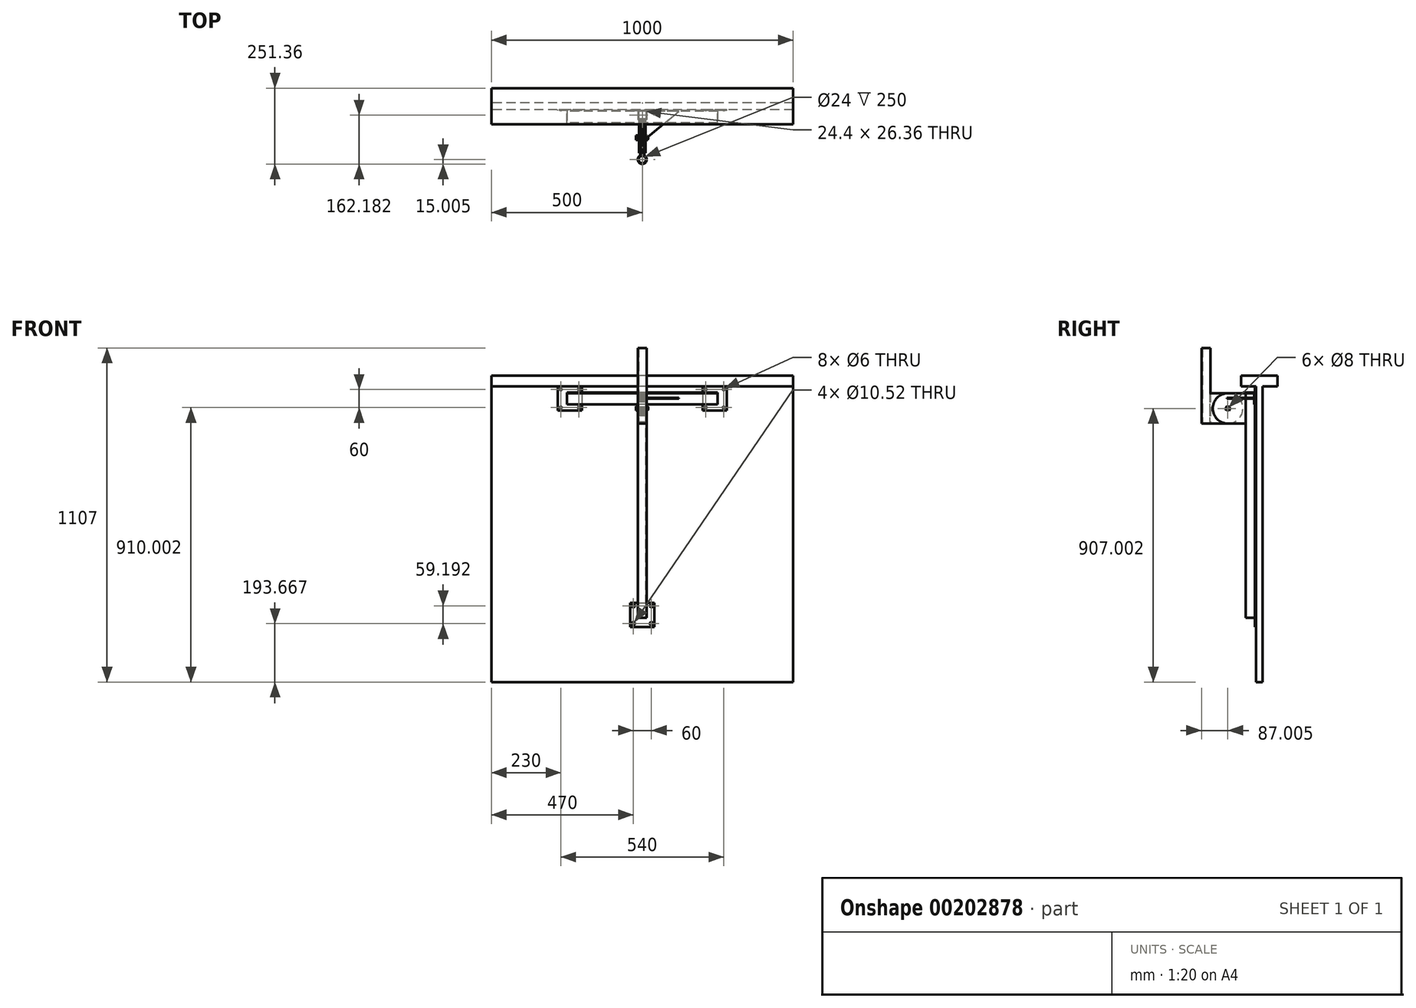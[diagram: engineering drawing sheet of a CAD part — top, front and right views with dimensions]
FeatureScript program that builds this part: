
annotation { "Feature Type Name" : "Feature", "Feature Type Description" : "" }
export const myFeature = defineFeature(function(context is Context, id is Id, definition is map)
    precondition{}
    {
        {
            assignVariable(context, id + "F0", {"name" : "PlateWidth", "anyValue" : 100});
        }
        {
            var Q0;
            Q0=qCreatedBy(makeId("Right.planeOp"),FACE);
            var sketch = newSketch(context, id + "F1", { "sketchPlane" : qUnion([Q0])});
            skLineSegment(sketch, "E0", {"start": v(0, 214.68) * mm, "end": v(0, -692.13) * mm, "construction": true});
            skLineSegment(sketch, "E1", {"start": v(109.52, 0) * mm, "end": v(-182.78, 0) * mm, "construction": true});
            skLineSegment(sketch, "E2", {"start": v(60, 146.82) * mm, "end": v(11, 146.82) * mm});
            skLineSegment(sketch, "E3", {"start": v(-60, 181.82) * mm, "end": v(-60, 146.82) * mm});
            skLineSegment(sketch, "E4", {"start": v(60, 181.82) * mm, "end": v(-60, 181.82) * mm});
            skLineSegment(sketch, "E5", {"start": v(11, 146.82) * mm, "end": v(11, -833.18) * mm});
            skLineSegment(sketch, "E6", {"start": v(60, 181.82) * mm, "end": v(60, 146.82) * mm});
            skLineSegment(sketch, "E7", {"start": v(-11, 146.82) * mm, "end": v(-11, -833.18) * mm});
            skLineSegment(sketch, "E8.trimOffspring", {"start": v(-11, 146.82) * mm, "end": v(-60, 146.82) * mm});
            skLineSegment(sketch, "E9", {"start": v(11, -833.18) * mm, "end": v(-11, -833.18) * mm});
            skSolve(sketch);
        }
        {
            var Q0;
            Q0 = qSketchRegion(id + "F1", true);
            extrude(context, id + "F2", {"entities" : qUnion([Q0]), "endBound" : BoundingType.SYMMETRIC, "depth" : 1000 * mm});
        }
        {
            var Q0;
            Q0=makeQuery(id+"F2.opExtrude","SWEPT_FACE",FACE,{"disambiguationData":[OSD([sQuery(id+"F1.wireOp",EDGE,"E7")])]});
            var sketch = newSketch(context, id + "F3", { "sketchPlane" : qUnion([Q0])});
            skLineSegment(sketch, "E10.bottom", {"start": v(-280, 146.82) * mm, "end": v(-200, 146.82) * mm});
            skLineSegment(sketch, "E10.top", {"start": v(-280, 66.82) * mm, "end": v(-200, 66.82) * mm});
            skLineSegment(sketch, "E10.left", {"start": v(-280, 146.82) * mm, "end": v(-280, 66.82) * mm});
            skLineSegment(sketch, "E10.right", {"start": v(-200, 146.82) * mm, "end": v(-200, 66.82) * mm});
            skLineSegment(sketch, "E11.bottom", {"start": v(200, 146.82) * mm, "end": v(280, 146.82) * mm});
            skLineSegment(sketch, "E11.top", {"start": v(200, 66.82) * mm, "end": v(280, 66.82) * mm});
            skLineSegment(sketch, "E11.left", {"start": v(200, 146.82) * mm, "end": v(200, 66.82) * mm});
            skLineSegment(sketch, "E11.right", {"start": v(280, 146.82) * mm, "end": v(280, 66.82) * mm});
            skLineSegment(sketch, "E12.bottom", {"start": v(-40, -570.32) * mm, "end": v(40, -570.32) * mm});
            skLineSegment(sketch, "E12.top", {"start": v(-40, -650.32) * mm, "end": v(40, -650.32) * mm});
            skLineSegment(sketch, "E12.left", {"start": v(-40, -570.32) * mm, "end": v(-40, -650.32) * mm});
            skLineSegment(sketch, "E12.right", {"start": v(40, -570.32) * mm, "end": v(40, -650.32) * mm});
            skLineSegment(sketch, "E13", {"start": v(0, 299.9) * mm, "end": v(0, -676.48) * mm, "construction": true});
            skCircle(sketch, "E14", {"center": v(-270, 136.82) * mm, "radius": 3 * mm});
            skCircle(sketch, "E15", {"center": v(-270, 76.82) * mm, "radius": 3 * mm});
            skCircle(sketch, "E16", {"center": v(-210, 76.82) * mm, "radius": 3 * mm});
            skCircle(sketch, "E17", {"center": v(-210, 136.82) * mm, "radius": 3 * mm});
            skLineSegment(sketch, "E18", {"start": v(-326.35, 106.82) * mm, "end": v(-177.46, 106.82) * mm, "construction": true});
            skLineSegment(sketch, "E19", {"start": v(-240, 161.7) * mm, "end": v(-240, 23.33) * mm, "construction": true});
            skLineSegment(sketch, "E20", {"start": v(169.17, 106.82) * mm, "end": v(317.54, 106.82) * mm, "construction": true});
            skLineSegment(sketch, "E21", {"start": v(240, 194.74) * mm, "end": v(240, 20.69) * mm, "construction": true});
            skCircle(sketch, "E22", {"center": v(210, 136.82) * mm, "radius": 3 * mm});
            skCircle(sketch, "E23", {"center": v(210, 76.82) * mm, "radius": 3 * mm});
            skCircle(sketch, "E24", {"center": v(270, 76.82) * mm, "radius": 3 * mm});
            skCircle(sketch, "E25", {"center": v(270, 136.82) * mm, "radius": 3 * mm});
            skPoint(sketch, "E26", {"position": v(0, -650.32) * mm});
            skLineSegment(sketch, "E27", {"start": v(-86.42, -609.92) * mm, "end": v(73.18, -609.92) * mm, "construction": true});
            skCircle(sketch, "E28", {"center": v(-30, -580.32) * mm, "radius": 5.26 * mm});
            skCircle(sketch, "E29", {"center": v(-30, -639.51) * mm, "radius": 5.26 * mm});
            skCircle(sketch, "E30", {"center": v(30, -639.51) * mm, "radius": 5.26 * mm});
            skCircle(sketch, "E31", {"center": v(30, -580.32) * mm, "radius": 5.26 * mm});
            skSolve(sketch);
        }
        {
            var Q0;
            Q0 = qSketchRegion(id + "F3", true);
            extrude(context, id + "F4", {"entities" : qUnion([Q0]), "depth" : 3 * mm});
        }
        {
            var Q0;
            Q0=qCreatedBy(makeId("Right.planeOp"),FACE);
            var sketch = newSketch(context, id + "F5", { "sketchPlane" : qUnion([Q0])});
            skLineSegment(sketch, "E32", {"start": v(-54, 126.82) * mm, "end": v(-14, 126.82) * mm});
            skLineSegment(sketch, "E33", {"start": v(-14, 126.82) * mm, "end": v(-14, 86.82) * mm});
            skLineSegment(sketch, "E34", {"start": v(-14, 86.82) * mm, "end": v(-17, 86.82) * mm});
            skLineSegment(sketch, "E35", {"start": v(-17, 86.82) * mm, "end": v(-17, 123.82) * mm});
            skLineSegment(sketch, "E36", {"start": v(-17, 123.82) * mm, "end": v(-54, 123.82) * mm});
            skLineSegment(sketch, "E37", {"start": v(-54, 123.82) * mm, "end": v(-54, 126.82) * mm});
            skLineSegment(sketch, "E38", {"start": v(35.41, 106.82) * mm, "end": v(-115.42, 106.82) * mm, "construction": true});
            skSolve(sketch);
        }
        {
            var Q0;
            Q0 = qSketchRegion(id + "F5", true);
            extrude(context, id + "F6", {"entities" : qUnion([Q0]), "endBound" : BoundingType.SYMMETRIC, "depth" : 500 * mm});
        }
        {
            var Q0;
            Q0=qCreatedBy(makeId("Top.planeOp"),FACE);
            var sketch = newSketch(context, id + "F7", { "sketchPlane" : qUnion([Q0])});
            skLineSegment(sketch, "E39.bottom", {"start": v(14.2, -14) * mm, "end": v(-14.2, -14) * mm});
            skLineSegment(sketch, "E39.top", {"start": v(14.2, -44.36) * mm, "end": v(-14.2, -44.36) * mm});
            skLineSegment(sketch, "E39.left", {"start": v(14.2, -14) * mm, "end": v(14.2, -44.36) * mm});
            skLineSegment(sketch, "E39.right", {"start": v(-14.2, -14) * mm, "end": v(-14.2, -44.36) * mm});
            skPoint(sketch, "E39.middle", {"position": v(0, -29.18) * mm});
            skLineSegment(sketch, "E40.0", {"start": v(12.2, -42.36) * mm, "end": v(-12.2, -42.36) * mm});
            skLineSegment(sketch, "E40.1", {"start": v(12.2, -16) * mm, "end": v(12.2, -42.36) * mm});
            skLineSegment(sketch, "E40.2", {"start": v(12.2, -16) * mm, "end": v(-12.2, -16) * mm});
            skLineSegment(sketch, "E40.3", {"start": v(-12.2, -16) * mm, "end": v(-12.2, -42.36) * mm});
            skSolve(sketch);
        }
        {
            var Q0;
            Q0 = qSketchRegion(id + "F7", true);
            var Q1;
            Q1=makeQuery(id+"F6.opExtrude","SWEPT_FACE",FACE,{"disambiguationData":[OSD([sQuery(id+"F5.wireOp",EDGE,"E36")])]});
            extrude(context, id + "F8", {"entities" : qUnion([Q0]), "oppositeDirection" : true, "depth" : 620 * mm, "hasSecondDirection" : true, "secondDirectionBound" : SecondDirectionBoundingType.UP_TO_SURFACE, "secondDirectionOppositeDirection" : false, "secondDirectionBoundEntityFace" : qUnion([Q1]), "secondDirectionDepth" : 25 * mm});
        }
        {
            var Q0;
            Q0=makeQuery(id+"F8.opExtrude","SWEPT_FACE",FACE,{"disambiguationData":[OSD([sQuery(id+"F7.wireOp",EDGE,"E39.top")])]});
            var sketch = newSketch(context, id + "F9", { "sketchPlane" : qUnion([Q0])});
            skLineSegment(sketch, "E41", {"start": v(0, 131.43) * mm, "end": v(0, -20.64) * mm, "construction": true});
            skLineSegment(sketch, "E42.bottom", {"start": v(-4.5, 123.82) * mm, "end": v(-1.5, 123.82) * mm});
            skLineSegment(sketch, "E42.top", {"start": v(-4.5, 23.82) * mm, "end": v(-1.5, 23.82) * mm});
            skLineSegment(sketch, "E42.left", {"start": v(-4.5, 123.82) * mm, "end": v(-4.5, 23.82) * mm});
            skLineSegment(sketch, "E42.right", {"start": v(-1.5, 123.82) * mm, "end": v(-1.5, 23.82) * mm});
            skLineSegment(sketch, "E43.bottom", {"start": v(-10.5, 123.82) * mm, "end": v(-7.5, 123.82) * mm});
            skLineSegment(sketch, "E43.top", {"start": v(-10.5, 23.82) * mm, "end": v(-7.5, 23.82) * mm});
            skLineSegment(sketch, "E43.left", {"start": v(-10.5, 123.82) * mm, "end": v(-10.5, 23.82) * mm});
            skLineSegment(sketch, "E43.right", {"start": v(-7.5, 123.82) * mm, "end": v(-7.5, 23.82) * mm});
            skLineSegment(sketch, "E44.MirrorCS", {"start": v(4.5, 23.82) * mm, "end": v(1.5, 23.82) * mm});
            skLineSegment(sketch, "E45.MirrorCS", {"start": v(10.5, 123.82) * mm, "end": v(7.5, 123.82) * mm});
            skLineSegment(sketch, "E46.MirrorCS", {"start": v(10.5, 23.82) * mm, "end": v(7.5, 23.82) * mm});
            skLineSegment(sketch, "E47.MirrorCS", {"start": v(4.5, 123.82) * mm, "end": v(1.5, 123.82) * mm});
            skLineSegment(sketch, "E48.MirrorCS", {"start": v(4.5, 123.82) * mm, "end": v(4.5, 23.82) * mm});
            skLineSegment(sketch, "E49.MirrorCS", {"start": v(1.5, 123.82) * mm, "end": v(1.5, 23.82) * mm});
            skLineSegment(sketch, "E50.MirrorCS", {"start": v(10.5, 123.82) * mm, "end": v(10.5, 23.82) * mm});
            skLineSegment(sketch, "E51.MirrorCS", {"start": v(7.5, 123.82) * mm, "end": v(7.5, 23.82) * mm});
            skSolve(sketch);
        }
        {
            var Q0;
            Q0 = qSketchRegion(id + "F9", true);
            extrude(context, id + "F10", {"entities" : qUnion([Q0]), "depth" : (getVariable(context, 'PlateWidth') + 10) * mm});
        }
        {
            var Q0;
            Q0=makeQuery(id+"F10.opExtrude","CAP_EDGE",EDGE,{"disambiguationData":[OSD([sQuery(id+"F9.wireOp",EDGE,"E43.top")])],"isStart":false});
            var Q1;
            Q1=makeQuery(id+"F10.opExtrude","CAP_EDGE",EDGE,{"disambiguationData":[OSD([sQuery(id+"F9.wireOp",EDGE,"E42.top")])],"isStart":false});
            var Q2;
            Q2=makeQuery(id+"F10.opExtrude","CAP_EDGE",EDGE,{"disambiguationData":[OSD([sQuery(id+"F9.wireOp",EDGE,"E44.MirrorCS")])],"isStart":false});
            var Q3;
            Q3=makeQuery(id+"F10.opExtrude","CAP_EDGE",EDGE,{"disambiguationData":[OSD([sQuery(id+"F9.wireOp",EDGE,"E46.MirrorCS")])],"isStart":false});
            var Q4;
            Q4=makeQuery(id+"F10.opExtrude","CAP_EDGE",EDGE,{"disambiguationData":[OSD([sQuery(id+"F9.wireOp",EDGE,"E45.MirrorCS")])],"isStart":false});
            var Q5;
            Q5=makeQuery(id+"F10.opExtrude","CAP_EDGE",EDGE,{"disambiguationData":[OSD([sQuery(id+"F9.wireOp",EDGE,"E47.MirrorCS")])],"isStart":false});
            var Q6;
            Q6=makeQuery(id+"F10.opExtrude","CAP_EDGE",EDGE,{"disambiguationData":[OSD([sQuery(id+"F9.wireOp",EDGE,"E42.bottom")])],"isStart":false});
            var Q7;
            Q7=makeQuery(id+"F10.opExtrude","CAP_EDGE",EDGE,{"disambiguationData":[OSD([sQuery(id+"F9.wireOp",EDGE,"E43.bottom")])],"isStart":false});
            fillet(context, id + "F11", {"entities" : qUnion([Q0, Q1, Q2, Q3, Q4, Q5, Q6, Q7]), "radius" : (getVariable(context, 'PlateWidth') / 2) * mm, "tangentPropagation" : true, "allowEdgeOverflow" : false});
        }
        {
            var Q0;
            Q0=makeQuery(id+"F8.opExtrude","SWEPT_FACE",FACE,{"disambiguationData":[OSD([sQuery(id+"F7.wireOp",EDGE,"E39.top")])]});
            cPlane(context, id + "F12", {"entities" : qUnion([Q0]), "cplaneType" : CPlaneType.OFFSET, "offset" : (getVariable(context, 'PlateWidth') + 2 * 10) * mm, "width" : 150 * mm, "height" : 150 * mm});
        }
        {
            var Q0;
            Q0=qCreatedBy(id+"F12.planeOp",FACE);
            var sketch = newSketch(context, id + "F13", { "sketchPlane" : qUnion([Q0])});
            skLineSegment(sketch, "E52.bottom", {"start": v(-7.5, 123.82) * mm, "end": v(-4.5, 123.82) * mm});
            skLineSegment(sketch, "E52.top", {"start": v(-7.5, 23.82) * mm, "end": v(-4.5, 23.82) * mm});
            skLineSegment(sketch, "E52.left", {"start": v(-7.5, 123.82) * mm, "end": v(-7.5, 23.82) * mm});
            skLineSegment(sketch, "E52.right", {"start": v(-4.5, 123.82) * mm, "end": v(-4.5, 23.82) * mm});
            skLineSegment(sketch, "E53.bottom", {"start": v(-1.5, 123.82) * mm, "end": v(1.5, 123.82) * mm});
            skLineSegment(sketch, "E53.top", {"start": v(-1.5, 23.82) * mm, "end": v(1.5, 23.82) * mm});
            skLineSegment(sketch, "E53.left", {"start": v(-1.5, 123.82) * mm, "end": v(-1.5, 23.82) * mm});
            skLineSegment(sketch, "E53.right", {"start": v(1.5, 123.82) * mm, "end": v(1.5, 23.82) * mm});
            skLineSegment(sketch, "E54.bottom", {"start": v(4.5, 123.82) * mm, "end": v(7.5, 123.82) * mm});
            skLineSegment(sketch, "E54.top", {"start": v(4.5, 23.82) * mm, "end": v(7.5, 23.82) * mm});
            skLineSegment(sketch, "E54.left", {"start": v(4.5, 123.82) * mm, "end": v(4.5, 23.82) * mm});
            skLineSegment(sketch, "E54.right", {"start": v(7.5, 123.82) * mm, "end": v(7.5, 23.82) * mm});
            skLineSegment(sketch, "E55", {"start": v(0, 0) * mm, "end": v(0, 140.03) * mm, "construction": true});
            skLineSegment(sketch, "E56", {"start": v(0, 140.03) * mm, "end": v(-1.6, 140.03) * mm, "construction": true});
            skSolve(sketch);
        }
        {
            var Q0;
            Q0 = qSketchRegion(id + "F13", true);
            extrude(context, id + "F14", {"entities" : qUnion([Q0]), "oppositeDirection" : true, "depth" : (getVariable(context, 'PlateWidth') + 10) * mm});
        }
        {
            var Q0;
            Q0=makeQuery(id+"F14.opExtrude","CAP_EDGE",EDGE,{"disambiguationData":[OSD([sQuery(id+"F13.wireOp",EDGE,"E54.bottom")])],"isStart":false});
            var Q1;
            Q1=makeQuery(id+"F14.opExtrude","CAP_EDGE",EDGE,{"disambiguationData":[OSD([sQuery(id+"F13.wireOp",EDGE,"E53.bottom")])],"isStart":false});
            var Q2;
            Q2=makeQuery(id+"F14.opExtrude","CAP_EDGE",EDGE,{"disambiguationData":[OSD([sQuery(id+"F13.wireOp",EDGE,"E52.bottom")])],"isStart":false});
            var Q3;
            Q3=makeQuery(id+"F14.opExtrude","CAP_EDGE",EDGE,{"disambiguationData":[OSD([sQuery(id+"F13.wireOp",EDGE,"E54.top")])],"isStart":false});
            var Q4;
            Q4=makeQuery(id+"F14.opExtrude","CAP_EDGE",EDGE,{"disambiguationData":[OSD([sQuery(id+"F13.wireOp",EDGE,"E53.top")])],"isStart":false});
            var Q5;
            Q5=makeQuery(id+"F14.opExtrude","CAP_EDGE",EDGE,{"disambiguationData":[OSD([sQuery(id+"F13.wireOp",EDGE,"E52.top")])],"isStart":false});
            fillet(context, id + "F15", {"entities" : qUnion([Q0, Q1, Q2, Q3, Q4, Q5]), "radius" : (getVariable(context, 'PlateWidth') / 2) * mm, "tangentPropagation" : true, "allowEdgeOverflow" : false});
        }
        {
            var Q0;
            Q0=makeQuery(id+"F10.opExtrude","SWEPT_FACE",FACE,{"disambiguationData":[OSD([sQuery(id+"F9.wireOp",EDGE,"E43.left")])]});
            var sketch = newSketch(context, id + "F16", { "sketchPlane" : qUnion([Q0])});
            skCircle(sketch, "E57", {"center": v(104.36, 73.82) * mm, "radius": 4 * mm});
            skSolve(sketch);
        }
        {
            var Q0;
            Q0 = qSketchRegion(id + "F16", true);
            var Q1;
            Q1=makeQuery(id+"F10.opExtrude","SWEPT_FACE",FACE,{"disambiguationData":[OSD([sQuery(id+"F9.wireOp",EDGE,"E50.MirrorCS")])]});
            extrude(context, id + "F17", {"entities" : qUnion([Q0]), "operationType" : NewBodyOperationType.REMOVE, "endBound" : BoundingType.UP_TO_SURFACE, "oppositeDirection" : true, "endBoundEntityFace" : qUnion([Q1]), "depth" : 25 * mm});
        }
        {
            var Q0;
            Q0=makeQuery(id+"F14.opExtrude","SWEPT_FACE",FACE,{"disambiguationData":[OSD([sQuery(id+"F13.wireOp",EDGE,"E53.bottom")])]});
            var sketch = newSketch(context, id + "F18", { "sketchPlane" : qUnion([Q0])});
            skLineSegment(sketch, "E58", {"start": v(0, -110.15) * mm, "end": v(0, -179.58) * mm, "construction": true});
            skCircle(sketch, "E59", {"center": v(0, -176.36) * mm, "radius": 15 * mm});
            skCircle(sketch, "E60", {"center": v(0, -176.36) * mm, "radius": 12 * mm});
            skSolve(sketch);
        }
        {
            var Q0;
            Q0 = qSketchRegion(id + "F18", true);
            var Q1;
            Q1=makeQuery(id+"F14.opExtrude","SWEPT_FACE",FACE,{"disambiguationData":[OSD([sQuery(id+"F13.wireOp",EDGE,"E52.top")])]});
            extrude(context, id + "F19", {"entities" : qUnion([Q0]), "depth" : 150 * mm, "hasSecondDirection" : true, "secondDirectionBound" : SecondDirectionBoundingType.UP_TO_SURFACE, "secondDirectionOppositeDirection" : true, "secondDirectionBoundEntityFace" : qUnion([Q1]), "secondDirectionDepth" : 25 * mm});
        }
        {
            var Q0;
            Q0=makeQuery(id+"F10.opExtrude","SWEPT_FACE",FACE,{"disambiguationData":[OSD([sQuery(id+"F9.wireOp",EDGE,"E43.left")])]});
            var sketch = newSketch(context, id + "F20", { "sketchPlane" : qUnion([Q0])});
            skCircle(sketch, "E61", {"center": v(104.36, 73.82) * mm, "radius": 4 * mm});
            skSolve(sketch);
        }
        {
            var Q0;
            Q0 = qSketchRegion(id + "F20", true);
            extrude(context, id + "F21", {"entities" : qUnion([Q0]), "oppositeDirection" : true, "depth" : 30 * mm});
        }
        {
            var Q0;
            Q0=makeQuery(id+"F21.opExtrude","CAP_FACE",FACE,{"disambiguationData":[OSD([sQuery(id+"F20.wireOp",EDGE,"E61")])],"isStart":true});
            var sketch = newSketch(context, id + "F22", { "sketchPlane" : qUnion([Q0])});
            skCircle(sketch, "E62.cCircle", {"center": v(104.36, 73.82) * mm, "radius": 6.5 * mm, "construction": true});
            skLineSegment(sketch, "E62.0", {"start": v(111.85, 73.51) * mm, "end": v(107.84, 67.17) * mm});
            skLineSegment(sketch, "E62.1", {"start": v(107.84, 67.17) * mm, "end": v(100.34, 67.48) * mm});
            skLineSegment(sketch, "E62.2", {"start": v(100.34, 67.48) * mm, "end": v(96.86, 74.13) * mm});
            skLineSegment(sketch, "E62.3", {"start": v(96.86, 74.13) * mm, "end": v(100.87, 80.47) * mm});
            skLineSegment(sketch, "E62.4", {"start": v(100.87, 80.47) * mm, "end": v(108.37, 80.16) * mm});
            skLineSegment(sketch, "E62.5", {"start": v(108.37, 80.16) * mm, "end": v(111.85, 73.51) * mm});
            skPoint(sketch, "E62.0.midPoint", {"position": v(109.85, 70.34) * mm});
            skSolve(sketch);
        }
        {
            var Q0;
            Q0 = qSketchRegion(id + "F22", true);
            extrude(context, id + "F23", {"entities" : qUnion([Q0]), "operationType" : NewBodyOperationType.ADD, "depth" : 10 * mm});
        }
        {
            var Q0;
            Q0=makeQuery(id+"F10.opExtrude","SWEPT_FACE",FACE,{"disambiguationData":[OSD([sQuery(id+"F9.wireOp",EDGE,"E50.MirrorCS")])]});
            var sketch = newSketch(context, id + "F24", { "sketchPlane" : qUnion([Q0])});
            skCircle(sketch, "E63.cCircle", {"center": v(-104.36, 73.82) * mm, "radius": 6.5 * mm, "construction": true});
            skLineSegment(sketch, "E63.0", {"start": v(-96.92, 72.83) * mm, "end": v(-101.5, 66.88) * mm});
            skLineSegment(sketch, "E63.1", {"start": v(-101.5, 66.88) * mm, "end": v(-108.93, 67.87) * mm});
            skLineSegment(sketch, "E63.2", {"start": v(-108.93, 67.87) * mm, "end": v(-111.8, 74.81) * mm});
            skLineSegment(sketch, "E63.3", {"start": v(-111.8, 74.81) * mm, "end": v(-107.22, 80.76) * mm});
            skLineSegment(sketch, "E63.4", {"start": v(-107.22, 80.76) * mm, "end": v(-99.78, 79.77) * mm});
            skLineSegment(sketch, "E63.5", {"start": v(-99.78, 79.77) * mm, "end": v(-96.92, 72.83) * mm});
            skPoint(sketch, "E63.0.midPoint", {"position": v(-99.2, 69.86) * mm});
            skSolve(sketch);
        }
        {
            var Q0;
            Q0 = qSketchRegion(id + "F24", true);
            extrude(context, id + "F25", {"entities" : qUnion([Q0]), "depth" : 8 * mm});
        }
        {
            var Q0;
            Q0=makeQuery(id+"F6.opExtrude","SWEPT_FACE",FACE,{"disambiguationData":[OSD([sQuery(id+"F5.wireOp",EDGE,"E36")])]});
            cPlane(context, id + "F26", {"entities" : qUnion([Q0]), "cplaneType" : CPlaneType.OFFSET, "offset" : 15 * mm, "width" : 150 * mm, "height" : 150 * mm});
        }
        {
            var Q0;
            Q0=qCreatedBy(id+"F26.planeOp",FACE);
            var sketch = newSketch(context, id + "F27", { "sketchPlane" : qUnion([Q0])});
            skLineSegment(sketch, "E64", {"start": v(10.5, 107.74) * mm, "end": v(121.18, 17) * mm});
            skLineSegment(sketch, "E65", {"start": v(121.18, 17) * mm, "end": v(14.2, 17) * mm});
            skLineSegment(sketch, "E66", {"start": v(14.2, 17) * mm, "end": v(14.2, 44.36) * mm});
            skLineSegment(sketch, "E67", {"start": v(14.2, 44.36) * mm, "end": v(10.5, 44.36) * mm});
            skLineSegment(sketch, "E68", {"start": v(10.5, 44.36) * mm, "end": v(10.5, 107.74) * mm});
            skSolve(sketch);
        }
        {
            var Q0;
            Q0 = qSketchRegion(id + "F27", true);
            extrude(context, id + "F28", {"entities" : qUnion([Q0]), "depth" : 3 * mm});
        }
    });
